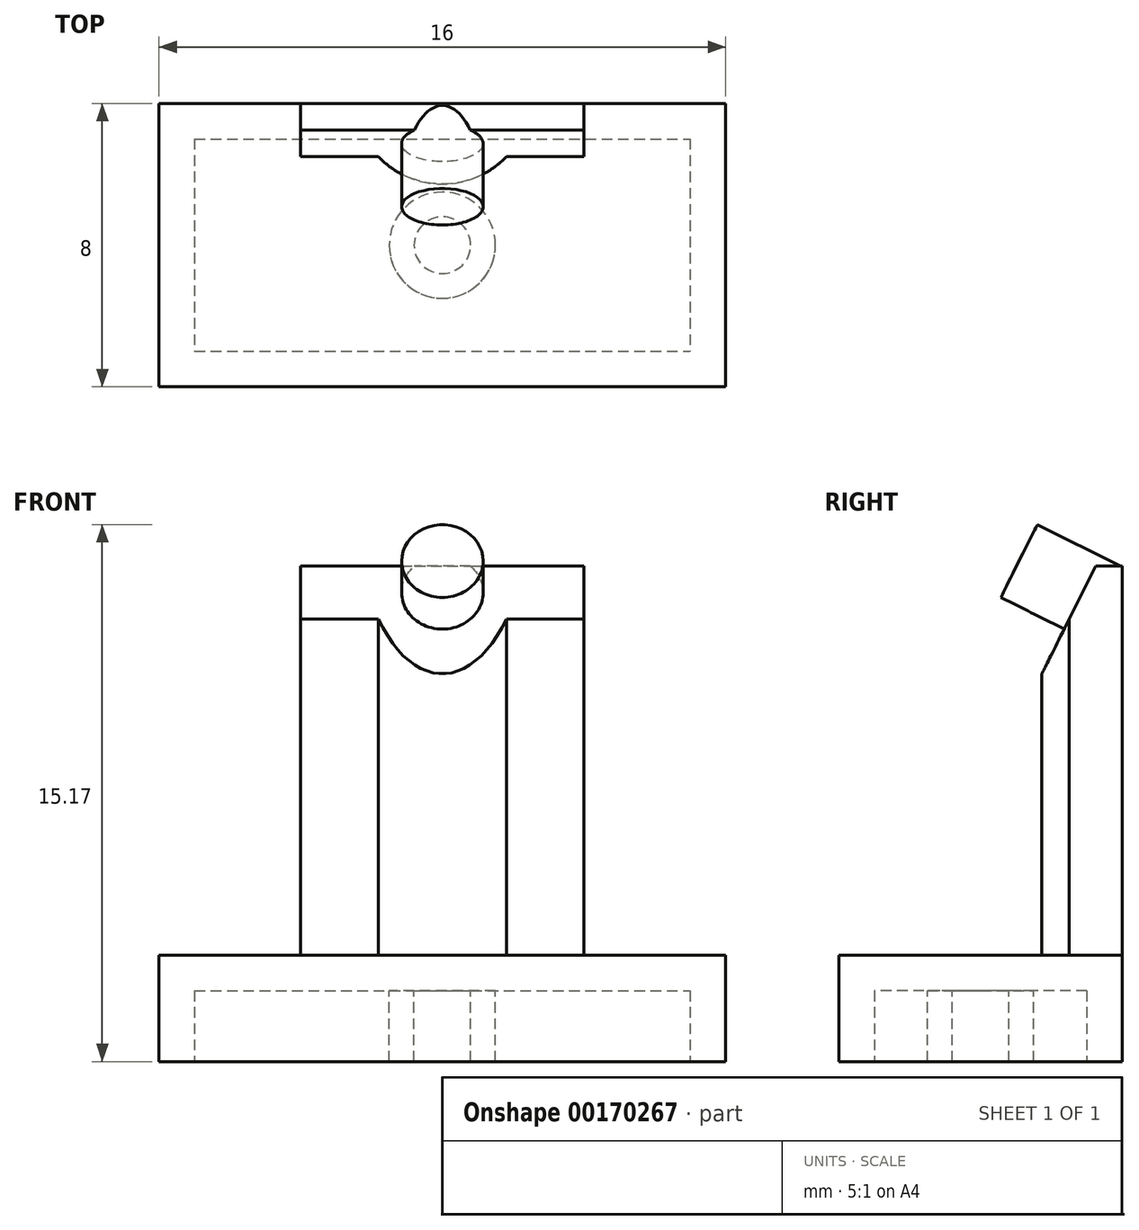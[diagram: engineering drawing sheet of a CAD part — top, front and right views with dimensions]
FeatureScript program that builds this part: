
annotation { "Feature Type Name" : "Feature", "Feature Type Description" : "" }
export const myFeature = defineFeature(function(context is Context, id is Id, definition is map)
    precondition{}
    {
        {
            var Q0;
            Q0=qCreatedBy(makeId("Top.planeOp"),FACE);
            var sketch = newSketch(context, id + "F0", { "sketchPlane" : qUnion([Q0])});
            skLineSegment(sketch, "E0.bottom", {"start": v(-8, 4) * mm, "end": v(8, 4) * mm});
            skLineSegment(sketch, "E0.top", {"start": v(-8, -4) * mm, "end": v(8, -4) * mm});
            skLineSegment(sketch, "E0.left", {"start": v(-8, 4) * mm, "end": v(-8, -4) * mm});
            skLineSegment(sketch, "E0.right", {"start": v(8, 4) * mm, "end": v(8, -4) * mm});
            skPoint(sketch, "E0.middle", {"position": v(0, 0) * mm});
            skSolve(sketch);
        }
        {
            var Q0;
            Q0 = qSketchRegion(id + "F0", true);
            extrude(context, id + "F1", {"entities" : qUnion([Q0]), "depth" : 3 * mm});
        }
        {
            var Q0;
            Q0=makeQuery(id+"F1.opExtrude","CAP_FACE",FACE,{"disambiguationData":[OSD([sQuery(id+"F0.wireOp",EDGE,"E0.bottom"),sQuery(id+"F0.wireOp",EDGE,"E0.top"),sQuery(id+"F0.wireOp",EDGE,"E0.left"),sQuery(id+"F0.wireOp",EDGE,"E0.right")])],"isStart":true});
            shell(context, id + "F2", {"entities" : qUnion([Q0]), "thickness" : 1 * mm});
        }
        {
            var Q0;
            Q0=makeQuery(id+"F2.opShell","OFFSET_FACE",FACE,{"disambiguationData":[OSD([sQuery(id+"F0.wireOp",EDGE,"E0.bottom"),sQuery(id+"F0.wireOp",EDGE,"E0.top"),sQuery(id+"F0.wireOp",EDGE,"E0.left"),sQuery(id+"F0.wireOp",EDGE,"E0.right")])]});
            var sketch = newSketch(context, id + "F3", { "sketchPlane" : qUnion([Q0])});
            skCircle(sketch, "E1", {"center": v(0, 0) * mm, "radius": 1.5 * mm});
            skCircle(sketch, "E2.0", {"center": v(0, 0) * mm, "radius": 0.8 * mm});
            skSolve(sketch);
        }
        {
            var Q0;
            Q0 = qSketchRegion(id + "F3", true);
            extrude(context, id + "F4", {"entities" : qUnion([Q0]), "operationType" : NewBodyOperationType.ADD, "depth" : 2 * mm});
        }
        {
            var Q0;
            Q0=makeQuery(id+"F1.opExtrude","CAP_FACE",FACE,{"disambiguationData":[OSD([sQuery(id+"F0.wireOp",EDGE,"E0.bottom"),sQuery(id+"F0.wireOp",EDGE,"E0.top"),sQuery(id+"F0.wireOp",EDGE,"E0.left"),sQuery(id+"F0.wireOp",EDGE,"E0.right")])],"isStart":false});
            var sketch = newSketch(context, id + "F5", { "sketchPlane" : qUnion([Q0])});
            skArc(sketch, "E3", {"start": v(0, 1.73) * mm, "mid": v(0.98, 1.93) * mm, "end": v(1.8, 2.5) * mm});
            skLineSegment(sketch, "E4", {"start": v(0, 4) * mm, "end": v(4, 4) * mm});
            skLineSegment(sketch, "E5", {"start": v(4, 4) * mm, "end": v(4, 2.5) * mm});
            skLineSegment(sketch, "E6", {"start": v(4, 2.5) * mm, "end": v(1.8, 2.5) * mm});
            skLineSegment(sketch, "E7.MirrorCS", {"start": v(0, 4) * mm, "end": v(-4, 4) * mm});
            skLineSegment(sketch, "E8.MirrorCS", {"start": v(-4, 2.5) * mm, "end": v(-1.8, 2.5) * mm});
            skLineSegment(sketch, "E9.MirrorCS", {"start": v(-4, 4) * mm, "end": v(-4, 2.5) * mm});
            skArc(sketch, "E10.MirrorCS", {"start": v(0, 1.73) * mm, "mid": v(-0.98, 1.93) * mm, "end": v(-1.8, 2.5) * mm});
            skSolve(sketch);
        }
        {
            var Q0;
            Q0 = qSketchRegion(id + "F5", true);
            extrude(context, id + "F6", {"entities" : qUnion([Q0]), "operationType" : NewBodyOperationType.ADD, "depth" : 11 * mm});
        }
        {
            var Q0;
            Q0=makeQuery(id+"F6.opExtrude","SWEPT_FACE",FACE,{"disambiguationData":[OSD([sQuery(id+"F5.wireOp",EDGE,"E5")])]});
            var sketch = newSketch(context, id + "F7", { "sketchPlane" : qUnion([Q0])});
            skLineSegment(sketch, "E11", {"start": v(3.25, 14) * mm, "end": v(1.25, 14) * mm});
            skLineSegment(sketch, "E12", {"start": v(1.25, 14) * mm, "end": v(1.25, 10) * mm});
            skLineSegment(sketch, "E13", {"start": v(1.25, 10) * mm, "end": v(3.25, 14) * mm});
            skSolve(sketch);
        }
        {
            var Q0;
            Q0 = qSketchRegion(id + "F7", true);
            extrude(context, id + "F8", {"entities" : qUnion([Q0]), "operationType" : NewBodyOperationType.REMOVE, "endBound" : BoundingType.THROUGH_ALL, "oppositeDirection" : true, "depth" : 25 * mm});
        }
        {
            var Q0;
            Q0=makeQuery(id+"F8.boolean.opBoolean","COPY",FACE,{"derivedFrom":makeQuery(id+"F8.opExtrude","SWEPT_FACE",FACE,{"disambiguationData":[OSD([sQuery(id+"F7.wireOp",EDGE,"E13")])]})});
            var sketch = newSketch(context, id + "F9", { "sketchPlane" : qUnion([Q0])});
            skCircle(sketch, "E14", {"center": v(0, 13.14) * mm, "radius": 1.15 * mm});
            skSolve(sketch);
        }
        {
            var Q0;
            Q0 = qSketchRegion(id + "F9", true);
            extrude(context, id + "F10", {"entities" : qUnion([Q0]), "operationType" : NewBodyOperationType.ADD, "endBound" : BoundingType.UP_TO_NEXT, "oppositeDirection" : true, "depth" : 25 * mm, "hasSecondDirection" : true, "secondDirectionOppositeDirection" : false, "secondDirectionDepth" : 2 * mm});
        }
    });
